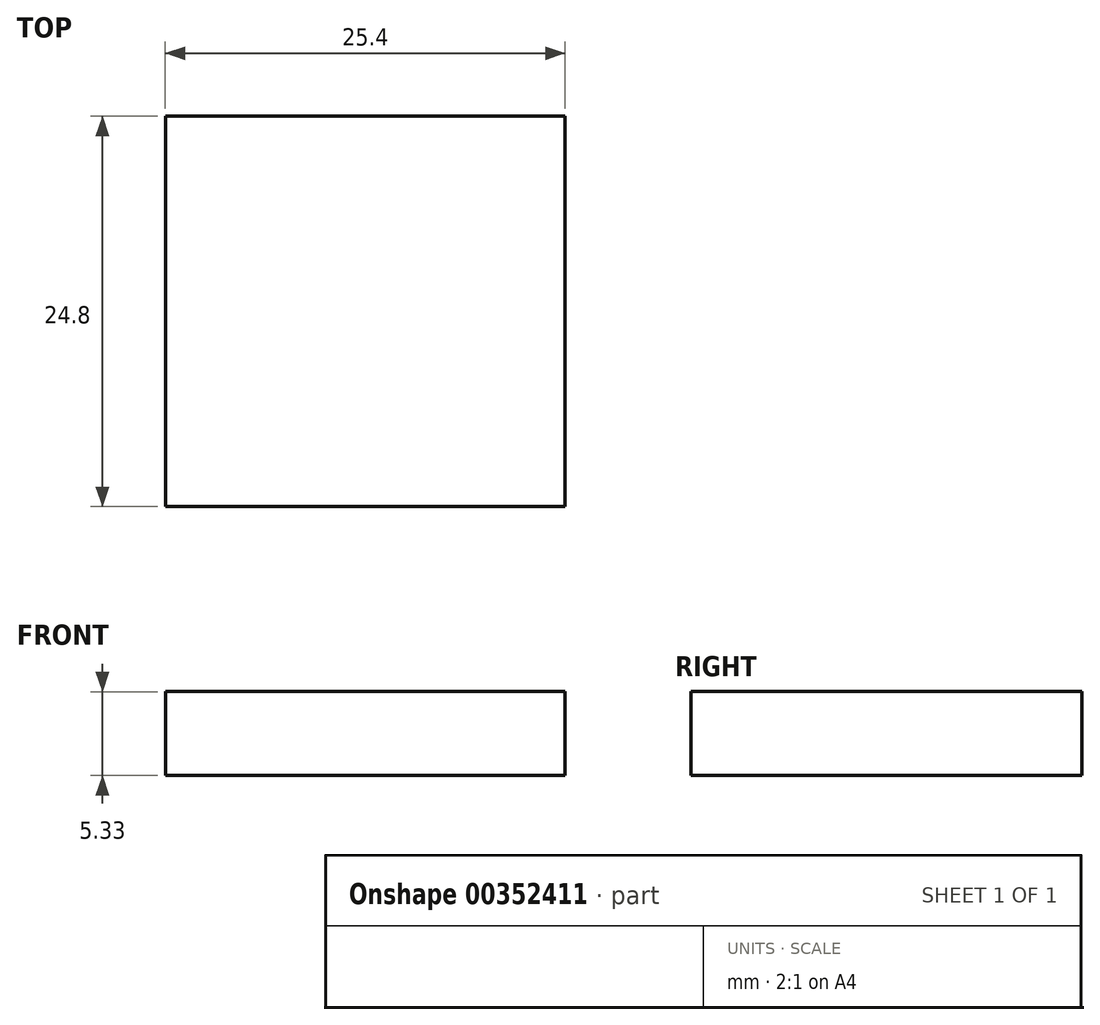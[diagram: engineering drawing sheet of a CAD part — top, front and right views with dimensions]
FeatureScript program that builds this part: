
annotation { "Feature Type Name" : "Feature", "Feature Type Description" : "" }
export const myFeature = defineFeature(function(context is Context, id is Id, definition is map)
    precondition{}
    {
        {
            var Q0;
            Q0=qCreatedBy(makeId("Top.planeOp"),FACE);
            var sketch = newSketch(context, id + "F0", { "sketchPlane" : qUnion([Q0])});
            skLineSegment(sketch, "E0.bottom", {"start": v(12.7, 12.4) * mm, "end": v(-12.7, 12.4) * mm});
            skLineSegment(sketch, "E0.top", {"start": v(12.7, -12.4) * mm, "end": v(-12.7, -12.4) * mm});
            skLineSegment(sketch, "E0.left", {"start": v(12.7, 12.4) * mm, "end": v(12.7, -12.4) * mm});
            skLineSegment(sketch, "E0.right", {"start": v(-12.7, 12.4) * mm, "end": v(-12.7, -12.4) * mm});
            skPoint(sketch, "E0.middle", {"position": v(0, 0) * mm});
            skSolve(sketch);
        }
        {
            var Q0;
            Q0=makeQuery(id+"F0.imprint","IMPRINT",FACE,{"disambiguationData":[TD([[makeQuery(id+"F0.imprint","IMPRINT",EDGE,{"derivedFrom":sQuery(id+"F0.wireOp",EDGE,"E0.bottom")}),1.0]])]});
            extrude(context, id + "F1", {"entities" : qUnion([Q0]), "depth" : 5.33 * mm});
        }
    });
